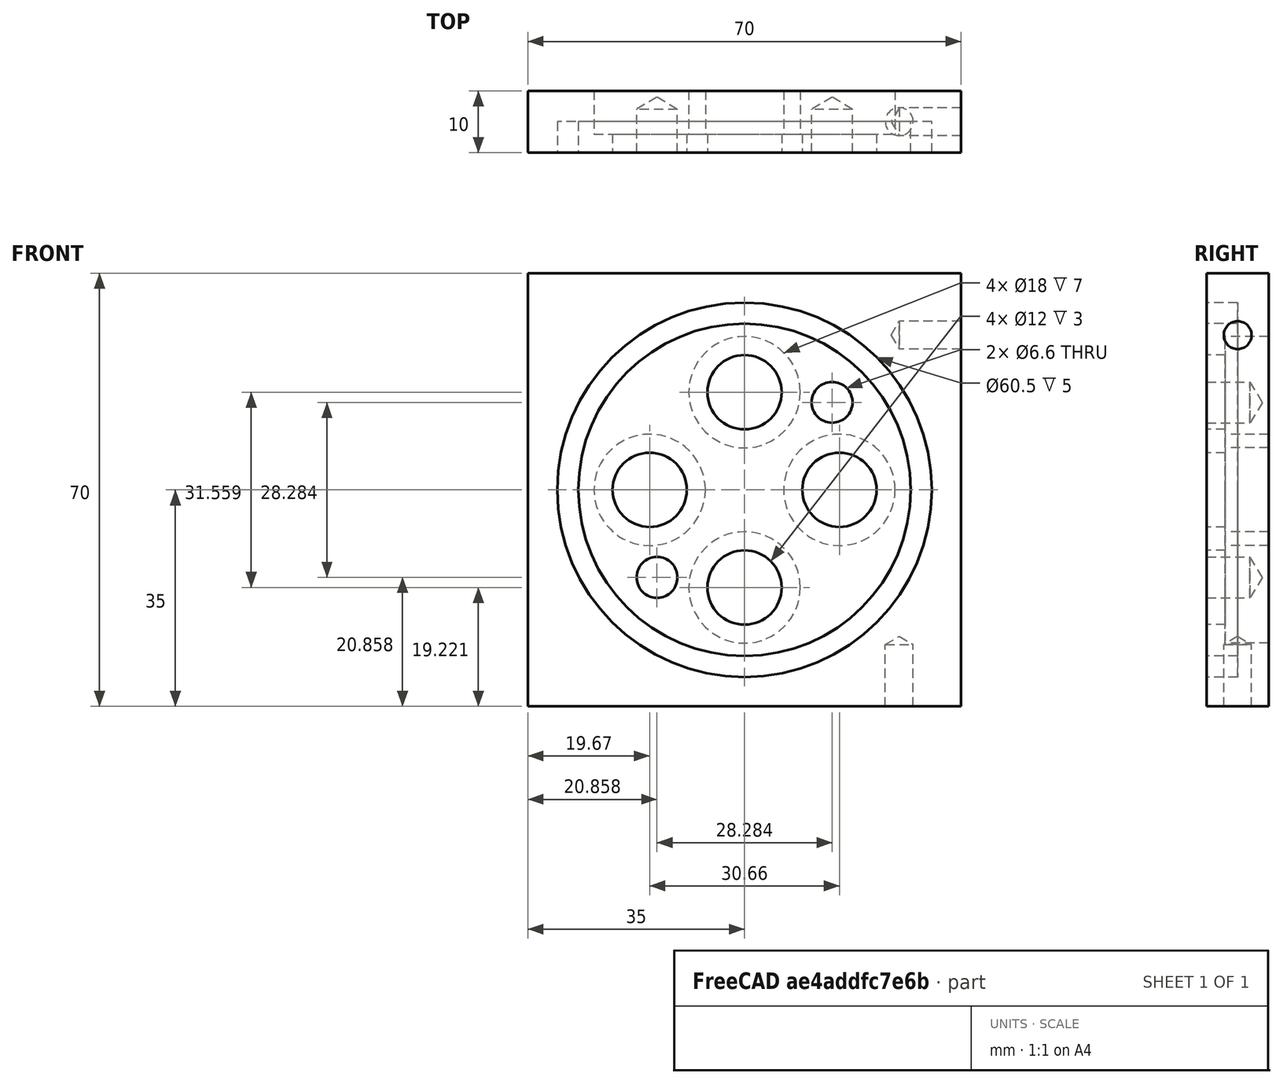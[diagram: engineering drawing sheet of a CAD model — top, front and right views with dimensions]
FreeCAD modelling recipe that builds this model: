
FCSTD DOCUMENT  (FreeCAD 0.21R33771 (Git))
Label: Deckelplatte Buttons
License: All rights reserved
LicenseURL: http://en.wikipedia.org/wiki/All_rights_reserved
objects: TechDraw::DrawViewDimension×13, Sketcher::SketchObject×7, TechDraw::DrawProjGroupItem×5, PartDesign::Hole×4, TechDraw::DrawViewSection×3, TechDraw::DrawViewAnnotation×2, PartDesign::Pad×1, PartDesign::Pocket×1, PartDesign::Body×1, TechDraw::DrawSVGTemplate×1, TechDraw::DrawProjGroup×1, TechDraw::DrawPage×1
note: 26 computed .brp shape members not serialized (recipe doc carries the construction recipe); baked Part::Feature solids carry a one-line shape summary decoded from their .brp

FEATURE [Sketcher::SketchObject] Sketch
  FullyConstrained = true
  MapMode = 5
  Placement = pos=(0,0,0) rot=(1,0,0;1.5708rad)
  Support = -> [XZ_Plane]
  sketch-geometry (4):
    g0: LineSegment StartX=-35 StartY=35 StartZ=0 EndX=35 EndY=35 EndZ=0
    g1: LineSegment StartX=35 StartY=35 StartZ=0 EndX=35 EndY=-35 EndZ=0
    g2: LineSegment StartX=35 StartY=-35 StartZ=0 EndX=-35 EndY=-35 EndZ=0
    g3: LineSegment StartX=-35 StartY=-35 StartZ=0 EndX=-35 EndY=35 EndZ=0
  constraints (10):
    c: Coincident(g0,g1)
    c: Coincident(g1,g2)
    c: Coincident(g2,g3)
    c: Coincident(g3,g0)
    c: Horizontal(g2)
    c: Vertical(g3)
    c: Symmetric(g0,g0,g-2)
    c: Symmetric(g0,g1,g-1)
    c: DistanceX(g0,g0) = 70
    c: Equal(g1,g0)
FEATURE [PartDesign::Pad] Pad
  Direction = (0,-1,-2e-16)
  Length = 10
  Length2 = 10
  Placement = pos=(0,0,0) rot=(1,0,0;1.5708rad)
  Profile = -> Sketch
  ReferenceAxis = -> Sketch [N_Axis]
  Type = 0
FEATURE [Sketcher::SketchObject] Sketch001
  FullyConstrained = true
  MapMode = 5
  Placement = pos=(0,-10,0) rot=(1,0,0;1.5708rad)
  Support = -> [Pad]
  sketch-geometry (2):
    g0: Circle CenterX=0 CenterY=0 CenterZ=0 NormalX=0 NormalY=0 NormalZ=1 AngleXU=0 Radius=26.85
    g1: Circle CenterX=0 CenterY=0 CenterZ=0 NormalX=0 NormalY=0 NormalZ=1 AngleXU=0 Radius=30.25
  constraints (4):
    c: Coincident(g0,g-1)
    c: Coincident(g1,g0)
    c: Diameter(g1) = 60.5
    c: Diameter(g0) = 53.7
FEATURE [PartDesign::Pocket] Pocket
  BaseFeature = -> Pad
  Direction = (0,1,2e-16)
  Length = 5
  Length2 = 5
  Placement = pos=(0,0,0) rot=(1,0,0;1.5708rad)
  Profile = -> Sketch001
  ReferenceAxis = -> Sketch001 [N_Axis]
  Type = 0
FEATURE [Sketcher::SketchObject] Sketch002
  FullyConstrained = true
  MapMode = 5
  Placement = pos=(0,-10,0) rot=(1,0,0;1.5708rad)
  Support = -> [Pocket]
FEATURE [Sketcher::SketchObject] Sketch003
  ExternalGeometry = -> [Pocket]
  FullyConstrained = true
  MapMode = 5
  Placement = pos=(35,0,0) rot=(0.707107,0,0.707107;3.14159rad)
  Support = -> [Pocket]
  sketch-geometry (1):
    g0: Circle CenterX=25 CenterY=5 CenterZ=0 NormalX=0 NormalY=0 NormalZ=1 AngleXU=0 Radius=2
  constraints (3):
    c: Diameter(g0) = 4
    c: DistanceY(g-1,g0) = 5
    c: DistanceX(g0,g-3) = 10
FEATURE [PartDesign::Hole] Hole
  BaseFeature = -> Pocket
  CustomThreadClearance = 0
  Depth = 10
  DepthType = 0
  Diameter = 4.5
  DrillForDepth = false
  DrillPoint = 1
  DrillPointAngle = 118
  HoleCutCountersinkAngle = 90
  HoleCutCustomValues = false
  HoleCutDepth = 0
  HoleCutDiameter = 6.1
  HoleCutType = 0
  ModelThread = false
  Placement = pos=(0,0,0) rot=(1,0,0;1.5708rad)
  Profile = -> Sketch003
  Tapered = false
  TaperedAngle = 90
  ThreadClass = 0
  ThreadDepth = 10
  ThreadDepthType = 0
  ThreadDirection = 0
  ThreadFit = 0
  ThreadSize = 11
  ThreadType = 1
  Threaded = false
  UseCustomThreadClearance = false
FEATURE [Sketcher::SketchObject] Sketch004
  ExternalGeometry = -> [Hole]
  FullyConstrained = true
  MapMode = 5
  Placement = pos=(0,-7.8e-15,-35) rot=(1,0,0;3.14159rad)
  Support = -> [Hole]
  sketch-geometry (1):
    g0: Circle CenterX=25 CenterY=5 CenterZ=0 NormalX=0 NormalY=0 NormalZ=1 AngleXU=0 Radius=2.5
  constraints (3):
    c: Diameter(g0) = 5
    c: DistanceX(g0,g-4) = 10
    c: DistanceY(g-5,g0) = 5
FEATURE [PartDesign::Hole] Hole001
  BaseFeature = -> Hole
  CustomThreadClearance = 0
  Depth = 10
  DepthType = 0
  Diameter = 4.5
  DrillForDepth = false
  DrillPoint = 1
  DrillPointAngle = 118
  HoleCutCountersinkAngle = 90
  HoleCutCustomValues = false
  HoleCutDepth = 0
  HoleCutDiameter = 6.1
  HoleCutType = 0
  ModelThread = false
  Placement = pos=(0,0,0) rot=(1,0,0;1.5708rad)
  Profile = -> Sketch004
  Tapered = false
  TaperedAngle = 90
  ThreadClass = 0
  ThreadDepth = 10
  ThreadDepthType = 0
  ThreadDirection = 0
  ThreadFit = 0
  ThreadSize = 11
  ThreadType = 1
  Threaded = false
  UseCustomThreadClearance = false
FEATURE [Sketcher::SketchObject] Sketch006
  ExternalGeometry = -> [Hole001]
  FullyConstrained = true
  MapMode = 5
  Placement = pos=(0,0,0) rot=(-1,0,0;1.5708rad)
  Support = -> [Hole001]
  sketch-geometry (4):
    g0: Circle CenterX=15.33 CenterY=0 CenterZ=0 NormalX=0 NormalY=0 NormalZ=1 AngleXU=0 Radius=6
    g1: Circle CenterX=0 CenterY=-15.7795 CenterZ=0 NormalX=0 NormalY=0 NormalZ=1 AngleXU=0 Radius=6
    g2: Circle CenterX=0 CenterY=15.7795 CenterZ=0 NormalX=0 NormalY=0 NormalZ=1 AngleXU=0 Radius=6
    g3: Circle CenterX=-15.33 CenterY=0 CenterZ=0 NormalX=0 NormalY=0 NormalZ=1 AngleXU=0 Radius=6
  constraints (10):
    c: PointOnObject(g3,g-1)
    c: Symmetric(g0,g3,g-1)
    c: PointOnObject(g1,g-2)
    c: Symmetric(g2,g1,g-1)
    c: Distance(g0,g2) = 22
    c: Diameter(g3) = 12
    c: Equal(g3,g2)
    c: Equal(g2,g0)
    c: Equal(g0,g1)
    c: DistanceX(g3,g0) = 30.66
FEATURE [PartDesign::Hole] Hole002
  BaseFeature = -> Hole001
  CustomThreadClearance = 0
  Depth = 200.987
  DepthType = 1
  Diameter = 12
  DrillForDepth = false
  DrillPoint = 1
  DrillPointAngle = 118
  HoleCutCountersinkAngle = 90
  HoleCutCustomValues = false
  HoleCutDepth = 7
  HoleCutDiameter = 18
  HoleCutType = 1
  ModelThread = false
  Placement = pos=(0,0,0) rot=(1,0,0;1.5708rad)
  Profile = -> Sketch006
  Tapered = false
  TaperedAngle = 90
  ThreadClass = 0
  ThreadDepth = 200.987
  ThreadDepthType = 0
  ThreadDirection = 0
  ThreadFit = 0
  ThreadSize = 0
  ThreadType = 0
  Threaded = false
  UseCustomThreadClearance = false
FEATURE [Sketcher::SketchObject] Sketch007
  ExternalGeometry = -> [Hole002]
  FullyConstrained = true
  MapMode = 5
  Placement = pos=(0,-10,2.2e-15) rot=(1,0,0;1.5708rad)
  Support = -> [Hole002]
  sketch-geometry (3):
    g0: LineSegment StartX=35 StartY=35 StartZ=0 EndX=-35 EndY=-35 EndZ=0
    g1: Circle CenterX=14.1421 CenterY=14.1421 CenterZ=0 NormalX=0 NormalY=0 NormalZ=1 AngleXU=0 Radius=3
    g2: Circle CenterX=-14.1421 CenterY=-14.1421 CenterZ=0 NormalX=0 NormalY=0 NormalZ=1 AngleXU=0 Radius=3
  constraints (7):
    c: Coincident(g0,g-3)
    c: Coincident(g0,g-4)
    c: PointOnObject(g1,g0)
    c: Diameter(g1) = 6
    c: Symmetric(g1,g2,g-1)
    c: Distance(g2,g1) = 40
    c: Equal(g2,g1)
FEATURE [PartDesign::Hole] Hole003
  BaseFeature = -> Hole002
  CustomThreadClearance = 0
  Depth = 7
  DepthType = 0
  Diameter = 6.6
  DrillForDepth = false
  DrillPoint = 1
  DrillPointAngle = 118
  HoleCutCountersinkAngle = 90
  HoleCutCustomValues = false
  HoleCutDepth = 0
  HoleCutDiameter = 6.1
  HoleCutType = 0
  ModelThread = false
  Placement = pos=(0,0,0) rot=(1,0,0;1.5708rad)
  Profile = -> Sketch007
  Tapered = false
  TaperedAngle = 90
  ThreadClass = 0
  ThreadDepth = 7
  ThreadDepthType = 0
  ThreadDirection = 0
  ThreadFit = 0
  ThreadSize = 14
  ThreadType = 1
  Threaded = false
  UseCustomThreadClearance = false
FEATURE [PartDesign::Body] Body
  Group = -> [Sketch,Pad,Sketch001,Pocket,Sketch002,Sketch003,Hole,Sketch004,Hole001,Sketch006,Hole002,Sketch007,Hole003]
  Origin = -> Origin
  Tip = -> Hole003
FEATURE [TechDraw::DrawSVGTemplate] Template
  EditableTexts = Approved1=Approved 1; Approved2=Approved 2; CheckedBy=Checked By; Code=Code; DrawingNumber=Drawing Number; DrawingTitle1=CANSpy; DrawingTitle2=Side Plate; DrawingTitle3=Button Plate; DrawnBy=Drawn By; Revision=Rev; Scale=Scale; Sheet=Sheet n of m; Weight=Weight
  Height = 279.4
  Orientation = 1
  Width = 431.8
FEATURE [TechDraw::DrawProjGroupItem] ProjItem  label="Front"
  CoarseView = false
  Direction = (0,-1,0)
  Focus = 100
  HardHidden = false
  IsoCount = 0
  IsoHidden = false
  IsoVisible = false
  LockPosition = true
  Perspective = false
  Rotation = 0
  RotationVector = (1,0,0)
  ScaleType = 2
  ScrubCount = 0
  SeamHidden = false
  SeamVisible = true
  SmoothHidden = false
  SmoothVisible = true
  Source = -> [Body]
  Type = 0
  X = 0
  XDirection = (1,0,0)
  Y = 0
FEATURE [TechDraw::DrawProjGroupItem] ProjItem001  label="Bottom"
  CoarseView = false
  Direction = (0,0,-1)
  Focus = 100
  HardHidden = false
  IsoCount = 0
  IsoHidden = false
  IsoVisible = false
  LockPosition = false
  Perspective = false
  Rotation = 0
  RotationVector = (1,0,0)
  ScaleType = 2
  ScrubCount = 0
  SeamHidden = false
  SeamVisible = true
  SmoothHidden = false
  SmoothVisible = true
  Source = -> [Body]
  Type = 5
  X = 0
  XDirection = (1,0,0)
  Y = 55
FEATURE [TechDraw::DrawProjGroupItem] ProjItem002  label="Top"
  CoarseView = false
  Direction = (0,0,1)
  Focus = 100
  HardHidden = false
  IsoCount = 0
  IsoHidden = false
  IsoVisible = false
  LockPosition = false
  Perspective = false
  Rotation = 0
  RotationVector = (1,0,0)
  ScaleType = 2
  ScrubCount = 0
  SeamHidden = false
  SeamVisible = true
  SmoothHidden = false
  SmoothVisible = true
  Source = -> [Body]
  Type = 4
  X = 0
  XDirection = (1,0,0)
  Y = -55
FEATURE [TechDraw::DrawViewSection] SectionView  label="Section  - "
  BaseView = -> ProjItem002
  CoarseView = false
  CutSurfaceDisplay = 2
  Direction = (0,-1,0)
  FileGeomPattern = <path>
  FileHatchPattern = <path>
  Focus = 100
  FuseBeforeCut = false
  HardHidden = false
  HatchOffset = (0,0,0)
  HatchRotation = 0
  HatchScale = 1
  IsoCount = 0
  IsoHidden = false
  IsoVisible = false
  LockPosition = false
  NameGeomPattern = Diamond
  Perspective = false
  Rotation = 0
  ScaleType = 2
  ScrubCount = 0
  SeamHidden = false
  SeamVisible = true
  SectionDirection = 2
  SectionNormal = (0,-1,0)
  SectionOrigin = (0.008,-5,-0.008)
  SmoothHidden = false
  SmoothVisible = true
  Source = -> [Body]
  TrimAfterCut = false
  X = 74.4423
  XDirection = (1,0,0)
  Y = 140.586
FEATURE [TechDraw::DrawViewSection] SectionView001  label="Section  - 001"
  BaseView = -> ProjItem
  CoarseView = false
  CutSurfaceDisplay = 2
  Direction = (0,0,-1)
  FileGeomPattern = <path>
  FileHatchPattern = <path>
  Focus = 100
  FuseBeforeCut = false
  HardHidden = false
  HatchOffset = (0,0,0)
  HatchRotation = 0
  HatchScale = 1
  IsoCount = 0
  IsoHidden = false
  IsoVisible = false
  LockPosition = false
  NameGeomPattern = Diamond
  Perspective = false
  Rotation = 0
  ScaleType = 2
  ScrubCount = 0
  SeamHidden = false
  SeamVisible = true
  SectionDirection = 2
  SectionNormal = (0,0,-1)
  SectionOrigin = (0.008,-5,-0.008)
  SmoothHidden = false
  SmoothVisible = true
  Source = -> [Body]
  TrimAfterCut = false
  X = 207.9
  XDirection = (1,0,0)
  Y = 192.7
FEATURE [TechDraw::DrawProjGroupItem] ProjItem005  label="Right"
  CoarseView = false
  Direction = (1,-1e-16,0)
  Focus = 100
  HardHidden = false
  IsoCount = 0
  IsoHidden = false
  IsoVisible = false
  LockPosition = false
  Perspective = false
  Rotation = 0
  RotationVector = (1,0,0)
  ScaleType = 2
  ScrubCount = 0
  SeamHidden = false
  SeamVisible = true
  SmoothHidden = false
  SmoothVisible = true
  Source = -> [Body]
  Type = 2
  X = -55
  XDirection = (1e-16,1,0)
  Y = 0
FEATURE [TechDraw::DrawViewAnnotation] Annotation
  Font = osifont
  LineSpace = 80
  LockPosition = false
  MaxWidth = -1
  Rotation = 0
  ScaleType = 0
  Text = M4 | blind hole
  TextSize = 5
  TextStyle = 0
  X = 232.559
  Y = 149.402
FEATURE [TechDraw::DrawViewAnnotation] Annotation001
  Font = osifont
  LineSpace = 80
  LockPosition = false
  MaxWidth = -1
  Rotation = 0
  ScaleType = 0
  Text = M4 | Blind hole
  TextSize = 5
  TextStyle = 0
  X = 142.32
  Y = 153.577
FEATURE [TechDraw::DrawViewDimension] Dimension004
  AngleOverride = false
  Arbitrary = false
  ArbitraryTolerances = false
  EqualTolerance = true
  ExtensionAngle = 0
  FormatSpec = %.2w
  FormatSpecOverTolerance = %+.2w
  FormatSpecUnderTolerance = %+.2w
  Inverted = false
  LineAngle = 0
  LockPosition = false
  MeasureType = 1
  OverTolerance = 0
  References2D = -> [SectionView001]
  Rotation = 0
  ScaleType = 0
  TheoreticalExact = false
  Type = 2
  UnderTolerance = 0
  X = -47.5103
  Y = 13.7509
FEATURE [TechDraw::DrawViewDimension] Dimension005
  AngleOverride = false
  Arbitrary = false
  ArbitraryTolerances = false
  EqualTolerance = true
  ExtensionAngle = 0
  FormatSpec = %.2w
  FormatSpecOverTolerance = %+.2w
  FormatSpecUnderTolerance = %+.2w
  Inverted = false
  LineAngle = 0
  LockPosition = false
  MeasureType = 1
  OverTolerance = 0
  References2D = -> [SectionView001]
  Rotation = 0
  ScaleType = 0
  TheoreticalExact = false
  Type = 2
  UnderTolerance = 0
  X = 40.038
  Y = 11.6026
FEATURE [TechDraw::DrawViewDimension] Dimension007
  AngleOverride = false
  Arbitrary = false
  ArbitraryTolerances = false
  EqualTolerance = true
  ExtensionAngle = 0
  FormatSpec = R%.2w
  FormatSpecOverTolerance = %+.2w
  FormatSpecUnderTolerance = %+.2w
  Inverted = false
  LineAngle = 0
  LockPosition = false
  MeasureType = 1
  OverTolerance = 0
  References2D = -> [ProjItem]
  Rotation = 0
  ScaleType = 0
  TheoreticalExact = false
  Type = 4
  UnderTolerance = 0
  X = 30.4294
  Y = -21.5303
FEATURE [TechDraw::DrawViewDimension] Dimension008
  AngleOverride = false
  Arbitrary = false
  ArbitraryTolerances = false
  EqualTolerance = true
  ExtensionAngle = 0
  FormatSpec = R%.2w
  FormatSpecOverTolerance = %+.2w
  FormatSpecUnderTolerance = %+.2w
  Inverted = false
  LineAngle = 0
  LockPosition = false
  MeasureType = 1
  OverTolerance = 0
  References2D = -> [ProjItem]
  Rotation = 0
  ScaleType = 0
  TheoreticalExact = false
  Type = 4
  UnderTolerance = 0
  X = 24.401
  Y = -25.8363
FEATURE [TechDraw::DrawViewDimension] Dimension009
  AngleOverride = false
  Arbitrary = false
  ArbitraryTolerances = false
  EqualTolerance = true
  ExtensionAngle = 0
  FormatSpec = %.2w
  FormatSpecOverTolerance = %+.2w
  FormatSpecUnderTolerance = %+.2w
  Inverted = false
  LineAngle = 0
  LockPosition = false
  MeasureType = 1
  OverTolerance = 0
  References2D = -> [SectionView]
  Rotation = 0
  ScaleType = 0
  TheoreticalExact = false
  Type = 2
  UnderTolerance = 0
  X = -44.6087
  Y = -17.3112
FEATURE [TechDraw::DrawViewDimension] Dimension010
  AngleOverride = false
  Arbitrary = false
  ArbitraryTolerances = false
  EqualTolerance = true
  ExtensionAngle = 0
  FormatSpec = %.2w
  FormatSpecOverTolerance = %+.2w
  FormatSpecUnderTolerance = %+.2w
  Inverted = false
  LineAngle = 0
  LockPosition = false
  MeasureType = 1
  OverTolerance = 0
  References2D = -> [ProjItem005]
  Rotation = 0
  ScaleType = 0
  TheoreticalExact = false
  Type = 2
  UnderTolerance = 0
  X = 14.703
  Y = 43.4517
FEATURE [TechDraw::DrawViewDimension] Dimension011
  AngleOverride = false
  Arbitrary = false
  ArbitraryTolerances = false
  EqualTolerance = true
  ExtensionAngle = 0
  FormatSpec = %.2w
  FormatSpecOverTolerance = %+.2w
  FormatSpecUnderTolerance = %+.2w
  Inverted = false
  LineAngle = 0
  LockPosition = false
  MeasureType = 1
  OverTolerance = 0
  References2D = -> [ProjItem]
  Rotation = 0
  ScaleType = 0
  TheoreticalExact = false
  Type = 2
  UnderTolerance = 0
  X = 41.0554
  Y = 23.3771
FEATURE [TechDraw::DrawViewDimension] Dimension012
  AngleOverride = false
  Arbitrary = false
  ArbitraryTolerances = false
  EqualTolerance = true
  ExtensionAngle = 0
  FormatSpec = %.2w
  FormatSpecOverTolerance = %+.2w
  FormatSpecUnderTolerance = %+.2w
  Inverted = false
  LineAngle = 0
  LockPosition = false
  MeasureType = 1
  OverTolerance = 0
  References2D = -> [ProjItem001]
  Rotation = 0
  ScaleType = 0
  TheoreticalExact = false
  Type = 2
  UnderTolerance = 0
  X = 39.4701
  Y = 14.2125
FEATURE [TechDraw::DrawProjGroupItem] ProjItem004  label="Rear"
  CoarseView = false
  Direction = (0,1,0)
  Focus = 100
  HardHidden = false
  IsoCount = 0
  IsoHidden = false
  IsoVisible = false
  LockPosition = true
  Perspective = false
  Rotation = 0
  RotationVector = (1,0,0)
  ScaleType = 2
  ScrubCount = 0
  SeamHidden = false
  SeamVisible = true
  SmoothHidden = false
  SmoothVisible = true
  Source = -> [Body]
  Type = 3
  X = 85.4231
  XDirection = (-1,0,0)
  Y = 0
FEATURE [TechDraw::DrawProjGroup] ProjGroup
  Anchor = -> ProjItem
  AutoDistribute = true
  LockPosition = false
  ProjectionType = 0
  Rotation = 0
  ScaleType = 0
  Source = -> [Body]
  Views = -> [ProjItem,ProjItem001,ProjItem002,ProjItem004,ProjItem005]
  X = 207.9
  Y = 139.7
  spacingX = 15
  spacingY = 15
FEATURE [TechDraw::DrawViewDimension] Dimension002
  AngleOverride = false
  Arbitrary = false
  ArbitraryTolerances = false
  EqualTolerance = true
  ExtensionAngle = 0
  FormatSpec = R%.2w
  FormatSpecOverTolerance = %+.2w
  FormatSpecUnderTolerance = %+.2w
  Inverted = false
  LineAngle = 0
  LockPosition = false
  MeasureType = 1
  OverTolerance = 0
  References2D = -> [ProjItem004]
  Rotation = 0
  ScaleType = 0
  TheoreticalExact = false
  Type = 4
  UnderTolerance = 0
  X = 22.6785
  Y = -22.9656
FEATURE [TechDraw::DrawViewDimension] Dimension003
  AngleOverride = false
  Arbitrary = false
  ArbitraryTolerances = false
  EqualTolerance = true
  ExtensionAngle = 0
  FormatSpec = R%.2w
  FormatSpecOverTolerance = %+.2w
  FormatSpecUnderTolerance = %+.2w
  Inverted = false
  LineAngle = 0
  LockPosition = false
  MeasureType = 1
  OverTolerance = 0
  References2D = -> [ProjItem004]
  Rotation = 0
  ScaleType = 0
  TheoreticalExact = false
  Type = 4
  UnderTolerance = 0
  X = 15.1573
  Y = -26.2956
FEATURE [TechDraw::DrawViewDimension] Dimension001
  AngleOverride = false
  Arbitrary = false
  ArbitraryTolerances = false
  EqualTolerance = true
  ExtensionAngle = 0
  FormatSpec = %.2w
  FormatSpecOverTolerance = %+.2w
  FormatSpecUnderTolerance = %+.2w
  Inverted = false
  LineAngle = 0
  LockPosition = false
  MeasureType = 1
  OverTolerance = 0
  References2D = -> [ProjItem004]
  Rotation = 0
  ScaleType = 0
  TheoreticalExact = false
  Type = 2
  UnderTolerance = 0
  X = 29.1031
  Y = 1.35992
FEATURE [TechDraw::DrawViewDimension] Dimension
  AngleOverride = false
  Arbitrary = false
  ArbitraryTolerances = false
  EqualTolerance = true
  ExtensionAngle = 0
  FormatSpec = %.2w
  FormatSpecOverTolerance = %+.2w
  FormatSpecUnderTolerance = %+.2w
  Inverted = false
  LineAngle = 0
  LockPosition = false
  MeasureType = 1
  OverTolerance = 0
  References2D = -> [ProjItem004]
  Rotation = 0
  ScaleType = 0
  TheoreticalExact = false
  Type = 2
  UnderTolerance = 0
  X = 51.7799
  Y = 1.72203
FEATURE [TechDraw::DrawViewSection] SectionView002  label="Section  - 002"
  BaseView = -> ProjItem004
  CoarseView = false
  CutSurfaceDisplay = 2
  Direction = (0,0,-1)
  FileGeomPattern = <path>
  FileHatchPattern = <path>
  Focus = 100
  FuseBeforeCut = false
  HardHidden = false
  HatchOffset = (0,0,0)
  HatchRotation = 0
  HatchScale = 1
  IsoCount = 0
  IsoHidden = false
  IsoVisible = false
  LockPosition = false
  NameGeomPattern = Diamond
  Perspective = false
  Rotation = 0
  ScaleType = 2
  ScrubCount = 0
  SeamHidden = false
  SeamVisible = true
  SectionDirection = 2
  SectionNormal = (0,0,-1)
  SectionOrigin = (0,-5,-12)
  SmoothHidden = false
  SmoothVisible = true
  Source = -> [Body]
  TrimAfterCut = false
  X = 292.9
  XDirection = (-1,0,0)
  Y = 192.7
FEATURE [TechDraw::DrawViewDimension] Dimension006
  AngleOverride = false
  Arbitrary = false
  ArbitraryTolerances = false
  EqualTolerance = true
  ExtensionAngle = 0
  FormatSpec = %.2w
  FormatSpecOverTolerance = %+.2w
  FormatSpecUnderTolerance = %+.2w
  Inverted = false
  LineAngle = 0
  LockPosition = false
  MeasureType = 1
  OverTolerance = 0
  References2D = -> [SectionView002]
  Rotation = 0
  ScaleType = 0
  TheoreticalExact = false
  Type = 2
  UnderTolerance = 0
  X = 16.3735
  Y = 15.0664
FEATURE [TechDraw::DrawPage] Page  label="2D-Drawing"
  KeepUpdated = true
  NextBalloonIndex = 1
  ProjectionType = 0
  Template = -> Template
  Views = -> [ProjGroup,SectionView,SectionView001,Dimension,Dimension001,Dimension002,Dimension003,SectionView002,Annotation,Annotation001,Dimension004,Dimension005,Dimension006,Dimension007,Dimension008,Dimension009,Dimension010,Dimension011,Dimension012]
note: 6 file-system paths scrubbed to <path> (originals preserved in the JSON sidecar)
